# Revit family: Basin-Wall_Mount-American_Standard-Regalyn-4869_Series
name_source: partatom
category: Plumbing Fixtures
revit_build: Autodesk Revit 2014 (Build: 20130308_1515(x64)
units: mm (PartAtom-declared; Revit-internal decimal feet)

## types (3) — shared parameters
Assembly Code = D2010310
Basin Shape = Rectangular
CW Connection = Yes
CWFU = 1.5
Cold Water Connection Diameter = 3/8"
Cold Water Connection Height = 11 1/4"
Cold Water Connection Radius = 3/16"
Cold Water Connection Width = 4"
Default Elevation = 34"
Description = American Standard Regalyn™ Wall-Mount Lavatory
Drain Length Location = 8"
HW Connection = Yes
HWFU = 1.5
Height = 7 5/8"
Hot Water Connection Diameter = 3/8"
Hot Water Connection Radius = 3/16"
Hot Water Connection Width = 4"
Installation Type = Wall Hung
Length = 17"
Manufacturer = American Standard
Material = Enameled-American Standard-Cast Iron
Product Documentation Link = https://www.americanstandard-us.com
Product Page URL = https://www.americanstandard-us.com
Revised Date = 01/20/2017
URL = http://www.americanstandard-us.com
Vent Connection = No
WFU = 2
Waste Connection = Yes
Waste Connection Radius = 5/8"
Width = 19"

## per-type parameters (varying)
| type | Faucet Hole Centerset | Faucet Holes |
| 4869.008 | 8" | Yes |
| 4869.004 | 4" | Yes |
| 4869.001 | 30" | No |

note: column(s) folded — value = type name in every type: Model

## geometry (parser evidence)
native form markers: Sweep x2
no freeform markers — native parametric forms only
